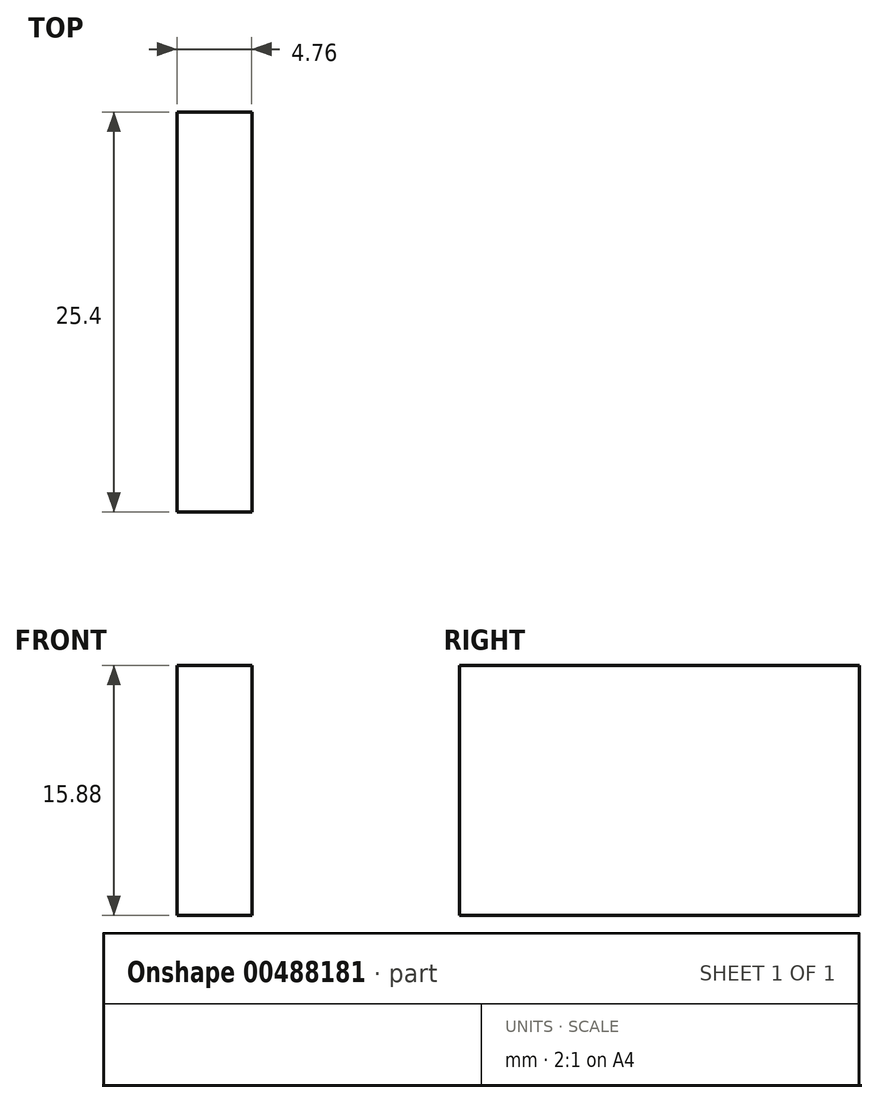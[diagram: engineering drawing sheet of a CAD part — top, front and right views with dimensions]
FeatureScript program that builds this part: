
annotation { "Feature Type Name" : "Feature", "Feature Type Description" : "" }
export const myFeature = defineFeature(function(context is Context, id is Id, definition is map)
    precondition{}
    {
        {
            var Q0;
            Q0=qCreatedBy(makeId("Front.planeOp"),FACE);
            var sketch = newSketch(context, id + "F0", { "sketchPlane" : qUnion([Q0])});
            skLineSegment(sketch, "E0", {"start": v(0, 0) * mm, "end": v(0, 15.88) * mm});
            skLineSegment(sketch, "E1", {"start": v(0, 15.88) * mm, "end": v(4.76, 15.88) * mm});
            skLineSegment(sketch, "E2", {"start": v(4.76, 15.88) * mm, "end": v(4.76, 0) * mm});
            skLineSegment(sketch, "E3", {"start": v(4.76, 0) * mm, "end": v(0, 0) * mm});
            skSolve(sketch);
        }
        {
            var Q0;
            Q0=makeQuery(id+"F0.imprint","IMPRINT",FACE,{"disambiguationData":[TD([[makeQuery(id+"F0.imprint","IMPRINT",EDGE,{"derivedFrom":sQuery(id+"F0.wireOp",EDGE,"E0")}),-1.0]])]});
            extrude(context, id + "F1", {"entities" : qUnion([Q0]), "depth" : 25.4 * mm});
        }
    });
